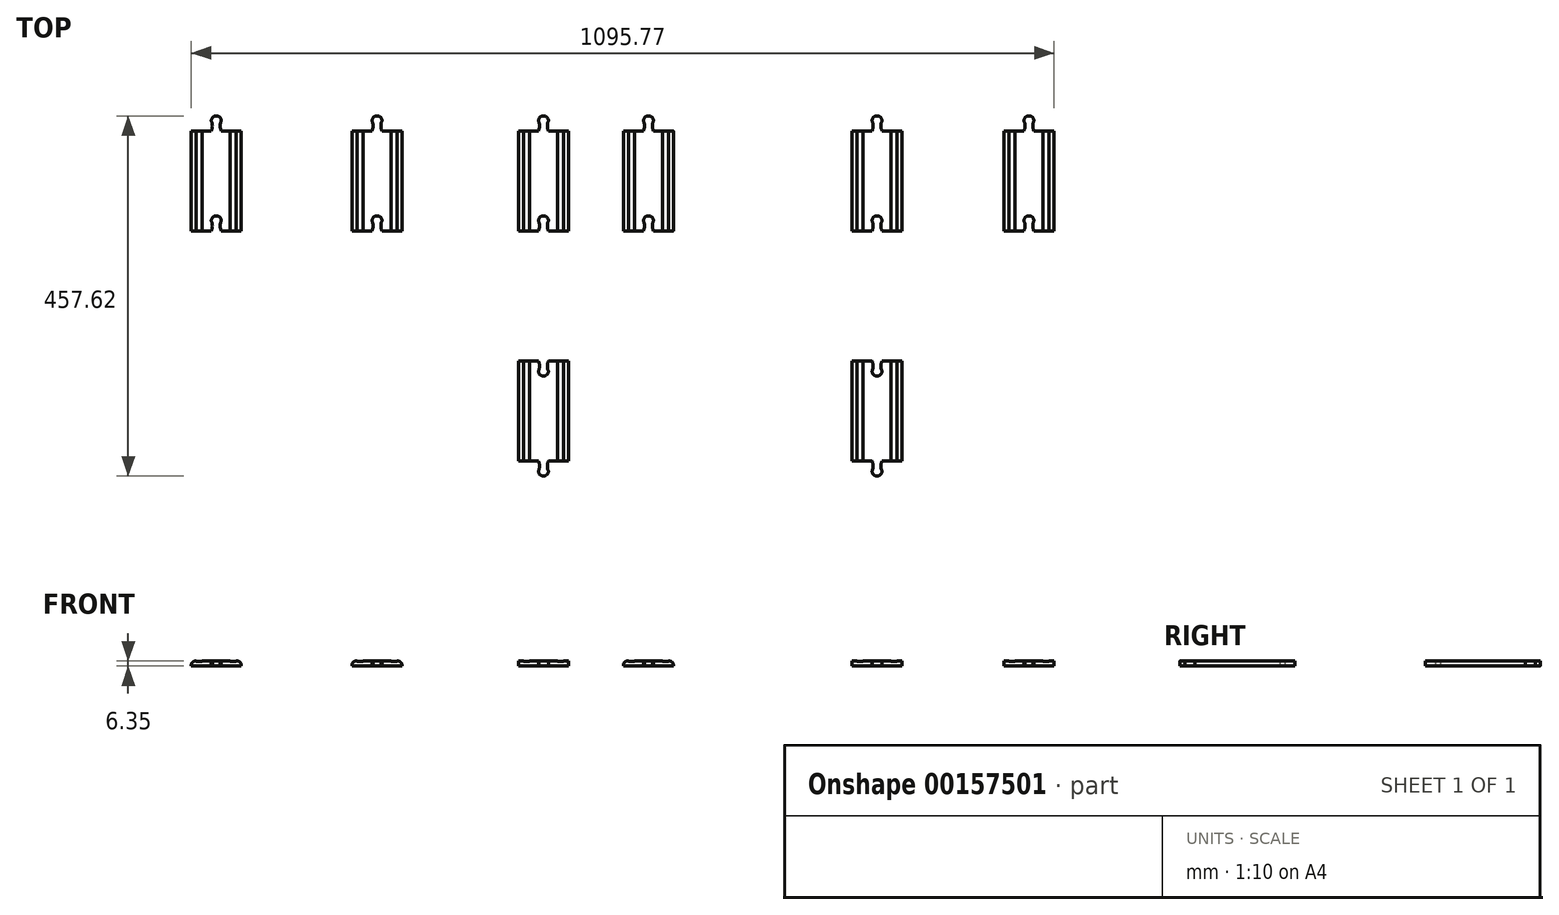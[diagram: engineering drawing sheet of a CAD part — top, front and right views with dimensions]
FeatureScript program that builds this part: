
annotation { "Feature Type Name" : "Feature", "Feature Type Description" : "" }
export const myFeature = defineFeature(function(context is Context, id is Id, definition is map)
    precondition{}
    {
        {
            var Q0;
            Q0=qCreatedBy(makeId("Top.planeOp"),FACE);
            var sketch = newSketch(context, id + "F0", { "sketchPlane" : qUnion([Q0])});
            skLineSegment(sketch, "E0", {"start": v(-44.88, 90.72) * mm, "end": v(-44.88, -36.28) * mm});
            skLineSegment(sketch, "E1", {"start": v(-44.88, -36.28) * mm, "end": v(-19.48, -36.28) * mm});
            skLineSegment(sketch, "E2", {"start": v(18.62, -36.28) * mm, "end": v(18.62, 90.72) * mm});
            skLineSegment(sketch, "E3", {"start": v(18.62, 90.72) * mm, "end": v(-6.78, 90.72) * mm});
            skArc(sketch, "E4", {"start": v(-6.78, 103.42) * mm, "mid": v(-13.13, 109.77) * mm, "end": v(-19.48, 103.42) * mm});
            skArc(sketch, "E5", {"start": v(-6.78, 103.42) * mm, "mid": v(-8.16, 97.07) * mm, "end": v(-6.78, 90.72) * mm});
            skArc(sketch, "E6.MirrorCS", {"start": v(-19.48, 103.42) * mm, "mid": v(-18.09, 97.07) * mm, "end": v(-19.48, 90.72) * mm});
            skArc(sketch, "E7", {"start": v(-6.78, -23.58) * mm, "mid": v(-13.13, -17.23) * mm, "end": v(-19.48, -23.58) * mm});
            skPoint(sketch, "E8.start.orphan", {"position": v(-13.13, -36.28) * mm});
            skArc(sketch, "E9", {"start": v(-6.78, -23.58) * mm, "mid": v(-8.16, -29.93) * mm, "end": v(-6.78, -36.28) * mm});
            skArc(sketch, "E10.MirrorCS", {"start": v(-19.48, -23.58) * mm, "mid": v(-18.09, -29.93) * mm, "end": v(-19.48, -36.28) * mm});
            skLineSegment(sketch, "E11.trimOffspring", {"start": v(-6.78, -36.28) * mm, "end": v(18.62, -36.28) * mm});
            skArc(sketch, "E12.MirrorCS", {"start": v(80.5, 103.42) * mm, "mid": v(81.9, 97.07) * mm, "end": v(80.5, 90.72) * mm});
            skLineSegment(sketch, "E13.MirrorCS", {"start": v(55.1, 90.72) * mm, "end": v(80.5, 90.72) * mm});
            skLineSegment(sketch, "E14.MirrorCS", {"start": v(118.6, 90.72) * mm, "end": v(118.6, -36.28) * mm});
            skLineSegment(sketch, "E15.MirrorCS", {"start": v(80.5, -36.28) * mm, "end": v(55.1, -36.28) * mm});
            skPoint(sketch, "E16.MirrorP", {"position": v(86.86, -36.28) * mm});
            skArc(sketch, "E17.MirrorCS", {"start": v(80.5, -23.58) * mm, "mid": v(81.9, -29.93) * mm, "end": v(80.5, -36.28) * mm});
            skArc(sketch, "E18.MirrorCS", {"start": v(80.5, 103.42) * mm, "mid": v(86.86, 109.77) * mm, "end": v(93.2, 103.42) * mm});
            skLineSegment(sketch, "E19.MirrorCS", {"start": v(55.1, -36.28) * mm, "end": v(55.1, 90.72) * mm});
            skArc(sketch, "E20.MirrorCS", {"start": v(93.2, -23.58) * mm, "mid": v(91.82, -29.93) * mm, "end": v(93.2, -36.28) * mm});
            skArc(sketch, "E21.MirrorCS", {"start": v(80.5, -23.58) * mm, "mid": v(86.86, -17.23) * mm, "end": v(93.2, -23.58) * mm});
            skLineSegment(sketch, "E22.MirrorCS", {"start": v(118.6, -36.28) * mm, "end": v(93.2, -36.28) * mm});
            skArc(sketch, "E23.MirrorCS", {"start": v(93.2, 103.42) * mm, "mid": v(91.82, 97.07) * mm, "end": v(93.2, 90.72) * mm});
            skArc(sketch, "E24.MirrorCS", {"start": v(197.37, -23.58) * mm, "mid": v(195.98, -29.93) * mm, "end": v(197.37, -36.28) * mm});
            skArc(sketch, "E25.MirrorCS", {"start": v(184.67, -23.58) * mm, "mid": v(186.06, -29.93) * mm, "end": v(184.67, -36.28) * mm});
            skArc(sketch, "E26.MirrorCS", {"start": v(184.67, 103.42) * mm, "mid": v(186.06, 97.07) * mm, "end": v(184.67, 90.72) * mm});
            skArc(sketch, "E27.MirrorCS", {"start": v(197.37, -23.58) * mm, "mid": v(191.02, -17.23) * mm, "end": v(184.67, -23.58) * mm});
            skArc(sketch, "E28.MirrorCS", {"start": v(197.37, 103.42) * mm, "mid": v(195.98, 97.07) * mm, "end": v(197.37, 90.72) * mm});
            skLineSegment(sketch, "E29.MirrorCS", {"start": v(197.37, -36.28) * mm, "end": v(222.77, -36.28) * mm});
            skArc(sketch, "E30.MirrorCS", {"start": v(197.37, 103.42) * mm, "mid": v(191.02, 109.77) * mm, "end": v(184.67, 103.42) * mm});
            skLineSegment(sketch, "E31.MirrorCS", {"start": v(159.27, -36.28) * mm, "end": v(184.67, -36.28) * mm});
            skLineSegment(sketch, "E32.MirrorCS", {"start": v(222.77, 90.72) * mm, "end": v(197.37, 90.72) * mm});
            skLineSegment(sketch, "E33.MirrorCS", {"start": v(222.77, -36.28) * mm, "end": v(222.77, 90.72) * mm});
            skPoint(sketch, "E34.MirrorP", {"position": v(191.02, -36.28) * mm});
            skLineSegment(sketch, "E35.MirrorCS", {"start": v(159.27, 90.72) * mm, "end": v(159.27, -36.28) * mm});
            skArc(sketch, "E36.MirrorCS", {"start": v(408.77, -23.58) * mm, "mid": v(407.39, -29.93) * mm, "end": v(408.77, -36.28) * mm});
            skArc(sketch, "E37.MirrorCS", {"start": v(396.07, -23.58) * mm, "mid": v(397.46, -29.93) * mm, "end": v(396.07, -36.28) * mm});
            skArc(sketch, "E38.MirrorCS", {"start": v(396.07, 103.42) * mm, "mid": v(402.42, 109.77) * mm, "end": v(408.77, 103.42) * mm});
            skLineSegment(sketch, "E39.MirrorCS", {"start": v(396.07, -36.28) * mm, "end": v(370.67, -36.28) * mm});
            skLineSegment(sketch, "E40.MirrorCS", {"start": v(434.17, -36.28) * mm, "end": v(408.77, -36.28) * mm});
            skArc(sketch, "E41.MirrorCS", {"start": v(396.07, -23.58) * mm, "mid": v(402.42, -17.23) * mm, "end": v(408.77, -23.58) * mm});
            skArc(sketch, "E42.MirrorCS", {"start": v(408.77, 103.42) * mm, "mid": v(407.39, 97.07) * mm, "end": v(408.77, 90.72) * mm});
            skArc(sketch, "E43.MirrorCS", {"start": v(396.07, 103.42) * mm, "mid": v(397.46, 97.07) * mm, "end": v(396.07, 90.72) * mm});
            skLineSegment(sketch, "E44.MirrorCS", {"start": v(370.67, 90.72) * mm, "end": v(396.07, 90.72) * mm});
            skLineSegment(sketch, "E45.MirrorCS", {"start": v(370.67, -36.28) * mm, "end": v(370.67, 90.72) * mm});
            skPoint(sketch, "E46.MirrorP", {"position": v(402.42, -36.28) * mm});
            skLineSegment(sketch, "E47.MirrorCS", {"start": v(434.17, 90.72) * mm, "end": v(434.17, -36.28) * mm});
            skArc(sketch, "E48.MirrorCS", {"start": v(542.2, 103.42) * mm, "mid": v(540.8, 97.07) * mm, "end": v(542.2, 90.72) * mm});
            skArc(sketch, "E49.MirrorCS", {"start": v(542.2, -23.58) * mm, "mid": v(540.8, -29.93) * mm, "end": v(542.2, -36.28) * mm});
            skArc(sketch, "E50.MirrorCS", {"start": v(542.2, 103.42) * mm, "mid": v(535.84, 109.77) * mm, "end": v(529.5, 103.42) * mm});
            skArc(sketch, "E51.MirrorCS", {"start": v(529.5, 103.42) * mm, "mid": v(530.88, 97.07) * mm, "end": v(529.5, 90.72) * mm});
            skArc(sketch, "E52.MirrorCS", {"start": v(529.5, -23.58) * mm, "mid": v(530.88, -29.93) * mm, "end": v(529.5, -36.28) * mm});
            skLineSegment(sketch, "E53.MirrorCS", {"start": v(567.6, 90.72) * mm, "end": v(542.2, 90.72) * mm});
            skArc(sketch, "E54.MirrorCS", {"start": v(542.2, -23.58) * mm, "mid": v(535.84, -17.23) * mm, "end": v(529.5, -23.58) * mm});
            skLineSegment(sketch, "E55.MirrorCS", {"start": v(504.1, -36.28) * mm, "end": v(529.5, -36.28) * mm});
            skLineSegment(sketch, "E56.MirrorCS", {"start": v(542.2, -36.28) * mm, "end": v(567.6, -36.28) * mm});
            skLineSegment(sketch, "E57.MirrorCS", {"start": v(504.1, 90.72) * mm, "end": v(504.1, -36.28) * mm});
            skLineSegment(sketch, "E58.MirrorCS", {"start": v(567.6, -36.28) * mm, "end": v(567.6, 90.72) * mm});
            skPoint(sketch, "E59.MirrorP", {"position": v(535.84, -36.28) * mm});
            skArc(sketch, "E60.MirrorCS", {"start": v(832.53, -23.58) * mm, "mid": v(831.14, -29.93) * mm, "end": v(832.53, -36.28) * mm});
            skArc(sketch, "E61.MirrorCS", {"start": v(819.83, -23.58) * mm, "mid": v(821.22, -29.93) * mm, "end": v(819.83, -36.28) * mm});
            skArc(sketch, "E62.MirrorCS", {"start": v(819.83, -23.58) * mm, "mid": v(826.18, -17.23) * mm, "end": v(832.53, -23.58) * mm});
            skLineSegment(sketch, "E63.MirrorCS", {"start": v(857.93, -36.28) * mm, "end": v(832.53, -36.28) * mm});
            skArc(sketch, "E64.MirrorCS", {"start": v(819.83, 103.42) * mm, "mid": v(821.22, 97.07) * mm, "end": v(819.83, 90.72) * mm});
            skArc(sketch, "E65.MirrorCS", {"start": v(832.53, 103.42) * mm, "mid": v(831.14, 97.07) * mm, "end": v(832.53, 90.72) * mm});
            skArc(sketch, "E66.MirrorCS", {"start": v(819.83, 103.42) * mm, "mid": v(826.18, 109.77) * mm, "end": v(832.53, 103.42) * mm});
            skLineSegment(sketch, "E67.MirrorCS", {"start": v(819.83, -36.28) * mm, "end": v(794.43, -36.28) * mm});
            skLineSegment(sketch, "E68.MirrorCS", {"start": v(794.43, 90.72) * mm, "end": v(819.83, 90.72) * mm});
            skPoint(sketch, "E69.MirrorP", {"position": v(826.18, -36.28) * mm});
            skLineSegment(sketch, "E70.MirrorCS", {"start": v(857.93, 90.72) * mm, "end": v(857.93, -36.28) * mm});
            skLineSegment(sketch, "E71.MirrorCS", {"start": v(794.43, -36.28) * mm, "end": v(794.43, 90.72) * mm});
            skArc(sketch, "E72.MirrorCS", {"start": v(819.83, -341.5) * mm, "mid": v(821.22, -335.15) * mm, "end": v(819.83, -328.8) * mm});
            skArc(sketch, "E73.MirrorCS", {"start": v(396.07, -214.5) * mm, "mid": v(397.46, -208.15) * mm, "end": v(396.07, -201.8) * mm});
            skArc(sketch, "E74.MirrorCS", {"start": v(93.2, -214.5) * mm, "mid": v(91.82, -208.15) * mm, "end": v(93.2, -201.8) * mm});
            skArc(sketch, "E75.MirrorCS", {"start": v(832.53, -341.5) * mm, "mid": v(831.14, -335.15) * mm, "end": v(832.53, -328.8) * mm});
            skArc(sketch, "E76.MirrorCS", {"start": v(408.77, -214.5) * mm, "mid": v(407.39, -208.15) * mm, "end": v(408.77, -201.8) * mm});
            skArc(sketch, "E77.MirrorCS", {"start": v(197.37, -214.5) * mm, "mid": v(191.02, -220.85) * mm, "end": v(184.67, -214.5) * mm});
            skArc(sketch, "E78.MirrorCS", {"start": v(80.5, -214.5) * mm, "mid": v(86.86, -220.85) * mm, "end": v(93.2, -214.5) * mm});
            skArc(sketch, "E79.MirrorCS", {"start": v(819.83, -341.5) * mm, "mid": v(826.18, -347.85) * mm, "end": v(832.53, -341.5) * mm});
            skArc(sketch, "E80.MirrorCS", {"start": v(819.83, -214.5) * mm, "mid": v(821.22, -208.15) * mm, "end": v(819.83, -201.8) * mm});
            skArc(sketch, "E81.MirrorCS", {"start": v(542.2, -214.5) * mm, "mid": v(540.8, -208.15) * mm, "end": v(542.2, -201.8) * mm});
            skArc(sketch, "E82.MirrorCS", {"start": v(197.37, -214.5) * mm, "mid": v(195.98, -208.15) * mm, "end": v(197.37, -201.8) * mm});
            skArc(sketch, "E83.MirrorCS", {"start": v(80.5, -214.5) * mm, "mid": v(81.9, -208.15) * mm, "end": v(80.5, -201.8) * mm});
            skArc(sketch, "E84.MirrorCS", {"start": v(832.53, -214.5) * mm, "mid": v(831.14, -208.15) * mm, "end": v(832.53, -201.8) * mm});
            skArc(sketch, "E85.MirrorCS", {"start": v(184.67, -214.5) * mm, "mid": v(186.06, -208.15) * mm, "end": v(184.67, -201.8) * mm});
            skArc(sketch, "E86.MirrorCS", {"start": v(529.5, -214.5) * mm, "mid": v(530.88, -208.15) * mm, "end": v(529.5, -201.8) * mm});
            skLineSegment(sketch, "E87.MirrorCS", {"start": v(197.37, -201.8) * mm, "end": v(222.77, -201.8) * mm});
            skArc(sketch, "E88.MirrorCS", {"start": v(542.2, -214.5) * mm, "mid": v(535.84, -220.85) * mm, "end": v(529.5, -214.5) * mm});
            skArc(sketch, "E89.MirrorCS", {"start": v(197.37, -341.5) * mm, "mid": v(195.98, -335.15) * mm, "end": v(197.37, -328.8) * mm});
            skLineSegment(sketch, "E90.MirrorCS", {"start": v(857.93, -201.8) * mm, "end": v(832.53, -201.8) * mm});
            skArc(sketch, "E91.MirrorCS", {"start": v(80.5, -341.5) * mm, "mid": v(86.86, -347.85) * mm, "end": v(93.2, -341.5) * mm});
            skLineSegment(sketch, "E92.MirrorCS", {"start": v(504.1, -201.8) * mm, "end": v(529.5, -201.8) * mm});
            skArc(sketch, "E93.MirrorCS", {"start": v(396.07, -341.5) * mm, "mid": v(402.42, -347.85) * mm, "end": v(408.77, -341.5) * mm});
            skArc(sketch, "E94.MirrorCS", {"start": v(542.2, -341.5) * mm, "mid": v(540.8, -335.15) * mm, "end": v(542.2, -328.8) * mm});
            skArc(sketch, "E95.MirrorCS", {"start": v(197.37, -341.5) * mm, "mid": v(191.02, -347.85) * mm, "end": v(184.67, -341.5) * mm});
            skLineSegment(sketch, "E96.MirrorCS", {"start": v(567.6, -328.8) * mm, "end": v(542.2, -328.8) * mm});
            skLineSegment(sketch, "E97.MirrorCS", {"start": v(370.67, -328.8) * mm, "end": v(396.07, -328.8) * mm});
            skArc(sketch, "E98.MirrorCS", {"start": v(819.83, -214.5) * mm, "mid": v(826.18, -220.85) * mm, "end": v(832.53, -214.5) * mm});
            skLineSegment(sketch, "E99.MirrorCS", {"start": v(396.07, -201.8) * mm, "end": v(370.67, -201.8) * mm});
            skLineSegment(sketch, "E100.MirrorCS", {"start": v(542.2, -201.8) * mm, "end": v(567.6, -201.8) * mm});
            skArc(sketch, "E101.MirrorCS", {"start": v(93.2, -341.5) * mm, "mid": v(91.82, -335.15) * mm, "end": v(93.2, -328.8) * mm});
            skArc(sketch, "E102.MirrorCS", {"start": v(396.07, -341.5) * mm, "mid": v(397.46, -335.15) * mm, "end": v(396.07, -328.8) * mm});
            skLineSegment(sketch, "E103.MirrorCS", {"start": v(794.43, -328.8) * mm, "end": v(819.83, -328.8) * mm});
            skArc(sketch, "E104.MirrorCS", {"start": v(529.5, -341.5) * mm, "mid": v(530.88, -335.15) * mm, "end": v(529.5, -328.8) * mm});
            skArc(sketch, "E105.MirrorCS", {"start": v(184.67, -341.5) * mm, "mid": v(186.06, -335.15) * mm, "end": v(184.67, -328.8) * mm});
            skArc(sketch, "E106.MirrorCS", {"start": v(396.07, -214.5) * mm, "mid": v(402.42, -220.85) * mm, "end": v(408.77, -214.5) * mm});
            skLineSegment(sketch, "E107.MirrorCS", {"start": v(55.1, -328.8) * mm, "end": v(80.5, -328.8) * mm});
            skLineSegment(sketch, "E108.MirrorCS", {"start": v(159.27, -201.8) * mm, "end": v(184.67, -201.8) * mm});
            skLineSegment(sketch, "E109.MirrorCS", {"start": v(80.5, -201.8) * mm, "end": v(55.1, -201.8) * mm});
            skLineSegment(sketch, "E110.MirrorCS", {"start": v(434.17, -201.8) * mm, "end": v(408.77, -201.8) * mm});
            skLineSegment(sketch, "E111.MirrorCS", {"start": v(819.83, -201.8) * mm, "end": v(794.43, -201.8) * mm});
            skArc(sketch, "E112.MirrorCS", {"start": v(408.77, -341.5) * mm, "mid": v(407.39, -335.15) * mm, "end": v(408.77, -328.8) * mm});
            skLineSegment(sketch, "E113.MirrorCS", {"start": v(222.77, -328.8) * mm, "end": v(197.37, -328.8) * mm});
            skArc(sketch, "E114.MirrorCS", {"start": v(80.5, -341.5) * mm, "mid": v(81.9, -335.15) * mm, "end": v(80.5, -328.8) * mm});
            skLineSegment(sketch, "E115.MirrorCS", {"start": v(118.6, -201.8) * mm, "end": v(93.2, -201.8) * mm});
            skArc(sketch, "E116.MirrorCS", {"start": v(542.2, -341.5) * mm, "mid": v(535.84, -347.85) * mm, "end": v(529.5, -341.5) * mm});
            skLineSegment(sketch, "E117.MirrorCS", {"start": v(434.17, -328.8) * mm, "end": v(434.17, -201.8) * mm});
            skLineSegment(sketch, "E118.MirrorCS", {"start": v(55.1, -201.8) * mm, "end": v(55.1, -328.8) * mm});
            skLineSegment(sketch, "E119.MirrorCS", {"start": v(370.67, -201.8) * mm, "end": v(370.67, -328.8) * mm});
            skPoint(sketch, "E120.MirrorP", {"position": v(86.86, -201.8) * mm});
            skLineSegment(sketch, "E121.MirrorCS", {"start": v(794.43, -201.8) * mm, "end": v(794.43, -328.8) * mm});
            skPoint(sketch, "E122.MirrorP", {"position": v(191.02, -201.8) * mm});
            skPoint(sketch, "E123.MirrorP", {"position": v(535.84, -201.8) * mm});
            skPoint(sketch, "E124.MirrorP", {"position": v(402.42, -201.8) * mm});
            skLineSegment(sketch, "E125.MirrorCS", {"start": v(567.6, -201.8) * mm, "end": v(567.6, -328.8) * mm});
            skLineSegment(sketch, "E126.MirrorCS", {"start": v(222.77, -201.8) * mm, "end": v(222.77, -328.8) * mm});
            skLineSegment(sketch, "E127.MirrorCS", {"start": v(118.6, -328.8) * mm, "end": v(118.6, -201.8) * mm});
            skPoint(sketch, "E128.MirrorP", {"position": v(826.18, -201.8) * mm});
            skLineSegment(sketch, "E129.MirrorCS", {"start": v(504.1, -328.8) * mm, "end": v(504.1, -201.8) * mm});
            skLineSegment(sketch, "E130.MirrorCS", {"start": v(159.27, -328.8) * mm, "end": v(159.27, -201.8) * mm});
            skLineSegment(sketch, "E131.MirrorCS", {"start": v(857.93, -328.8) * mm, "end": v(857.93, -201.8) * mm});
            skArc(sketch, "E132.MirrorCS", {"start": v(-6.78, -341.5) * mm, "mid": v(-13.13, -347.85) * mm, "end": v(-19.48, -341.5) * mm});
            skArc(sketch, "E133.MirrorCS", {"start": v(-19.48, -214.5) * mm, "mid": v(-18.09, -208.15) * mm, "end": v(-19.48, -201.8) * mm});
            skArc(sketch, "E134.MirrorCS", {"start": v(-6.78, -214.5) * mm, "mid": v(-13.13, -220.85) * mm, "end": v(-19.48, -214.5) * mm});
            skLineSegment(sketch, "E135.MirrorCS", {"start": v(-6.78, -201.8) * mm, "end": v(18.62, -201.8) * mm});
            skArc(sketch, "E136.MirrorCS", {"start": v(-6.78, -214.5) * mm, "mid": v(-8.16, -208.15) * mm, "end": v(-6.78, -201.8) * mm});
            skArc(sketch, "E137.MirrorCS", {"start": v(-19.48, -341.5) * mm, "mid": v(-18.09, -335.15) * mm, "end": v(-19.48, -328.8) * mm});
            skArc(sketch, "E138.MirrorCS", {"start": v(-6.78, -341.5) * mm, "mid": v(-8.16, -335.15) * mm, "end": v(-6.78, -328.8) * mm});
            skLineSegment(sketch, "E139.MirrorCS", {"start": v(18.62, -328.8) * mm, "end": v(-6.78, -328.8) * mm});
            skLineSegment(sketch, "E140.MirrorCS", {"start": v(-44.88, -201.8) * mm, "end": v(-19.48, -201.8) * mm});
            skLineSegment(sketch, "E141.MirrorCS", {"start": v(18.62, -201.8) * mm, "end": v(18.62, -328.8) * mm});
            skLineSegment(sketch, "E142.MirrorCS", {"start": v(-44.88, -328.8) * mm, "end": v(-44.88, -201.8) * mm});
            skPoint(sketch, "E143.MirrorP", {"position": v(-13.13, -201.8) * mm});
            skLineSegment(sketch, "E144.trimOffspring", {"start": v(-19.48, 90.72) * mm, "end": v(-44.88, 90.72) * mm});
            skLineSegment(sketch, "E145.trimOffspring", {"start": v(93.2, 90.72) * mm, "end": v(118.6, 90.72) * mm});
            skLineSegment(sketch, "E146.trimOffspring", {"start": v(184.67, 90.72) * mm, "end": v(159.27, 90.72) * mm});
            skLineSegment(sketch, "E147.trimOffspring", {"start": v(408.77, 90.72) * mm, "end": v(434.17, 90.72) * mm});
            skLineSegment(sketch, "E148.trimOffspring", {"start": v(529.5, 90.72) * mm, "end": v(504.1, 90.72) * mm});
            skLineSegment(sketch, "E149.trimOffspring", {"start": v(832.53, 90.72) * mm, "end": v(857.93, 90.72) * mm});
            skLineSegment(sketch, "E150.trimOffspring", {"start": v(832.53, -328.8) * mm, "end": v(857.93, -328.8) * mm});
            skLineSegment(sketch, "E151.trimOffspring", {"start": v(529.5, -328.8) * mm, "end": v(504.1, -328.8) * mm});
            skLineSegment(sketch, "E152.trimOffspring", {"start": v(408.77, -328.8) * mm, "end": v(434.17, -328.8) * mm});
            skLineSegment(sketch, "E153.trimOffspring", {"start": v(184.67, -328.8) * mm, "end": v(159.27, -328.8) * mm});
            skLineSegment(sketch, "E154.trimOffspring", {"start": v(93.2, -328.8) * mm, "end": v(118.6, -328.8) * mm});
            skLineSegment(sketch, "E155.trimOffspring", {"start": v(-19.48, -328.8) * mm, "end": v(-44.88, -328.8) * mm});
            skLineSegment(sketch, "E156", {"start": v(922.66, 120.17) * mm, "end": v(922.66, -61.86) * mm});
            skArc(sketch, "E157.MirrorCS", {"start": v(1025.49, -23.58) * mm, "mid": v(1024.1, -29.93) * mm, "end": v(1025.49, -36.28) * mm});
            skArc(sketch, "E158.MirrorCS", {"start": v(1012.79, -23.58) * mm, "mid": v(1014.17, -29.93) * mm, "end": v(1012.79, -36.28) * mm});
            skArc(sketch, "E159.MirrorCS", {"start": v(1025.49, 103.42) * mm, "mid": v(1024.1, 97.07) * mm, "end": v(1025.49, 90.72) * mm});
            skArc(sketch, "E160.MirrorCS", {"start": v(1012.79, 103.42) * mm, "mid": v(1014.17, 97.07) * mm, "end": v(1012.79, 90.72) * mm});
            skLineSegment(sketch, "E161.MirrorCS", {"start": v(1025.49, -36.28) * mm, "end": v(1050.89, -36.28) * mm});
            skLineSegment(sketch, "E162.MirrorCS", {"start": v(1050.89, 90.72) * mm, "end": v(1025.49, 90.72) * mm});
            skArc(sketch, "E163.MirrorCS", {"start": v(1025.49, -23.58) * mm, "mid": v(1019.14, -17.23) * mm, "end": v(1012.79, -23.58) * mm});
            skArc(sketch, "E164.MirrorCS", {"start": v(1025.49, 103.42) * mm, "mid": v(1019.14, 109.77) * mm, "end": v(1012.79, 103.42) * mm});
            skLineSegment(sketch, "E165.MirrorCS", {"start": v(1012.79, 90.72) * mm, "end": v(987.39, 90.72) * mm});
            skLineSegment(sketch, "E166.MirrorCS", {"start": v(987.39, -36.28) * mm, "end": v(1012.79, -36.28) * mm});
            skPoint(sketch, "E167.MirrorP", {"position": v(1019.14, -36.28) * mm});
            skLineSegment(sketch, "E168.MirrorCS", {"start": v(987.39, 90.72) * mm, "end": v(987.39, -36.28) * mm});
            skLineSegment(sketch, "E169.MirrorCS", {"start": v(1050.89, -36.28) * mm, "end": v(1050.89, 90.72) * mm});
            skSolve(sketch);
        }
        {
            var Q0;
            Q0=makeQuery(id+"F0.imprint","IMPRINT",FACE,{"disambiguationData":[TD([[makeQuery(id+"F0.imprint","IMPRINT",EDGE,{"derivedFrom":sQuery(id+"F0.wireOp",EDGE,"E0")}),1.0]])]});
            var Q1;
            Q1=makeQuery(id+"F0.imprint","IMPRINT",FACE,{"disambiguationData":[TD([[makeQuery(id+"F0.imprint","IMPRINT",EDGE,{"derivedFrom":sQuery(id+"F0.wireOp",EDGE,"E12.MirrorCS")}),1.0]])]});
            var Q2;
            Q2=makeQuery(id+"F0.imprint","IMPRINT",FACE,{"disambiguationData":[TD([[makeQuery(id+"F0.imprint","IMPRINT",EDGE,{"derivedFrom":sQuery(id+"F0.wireOp",EDGE,"E24.MirrorCS")}),1.0]])]});
            var Q3;
            Q3=makeQuery(id+"F0.imprint","IMPRINT",FACE,{"disambiguationData":[TD([[makeQuery(id+"F0.imprint","IMPRINT",EDGE,{"derivedFrom":sQuery(id+"F0.wireOp",EDGE,"E36.MirrorCS")}),1.0]])]});
            var Q4;
            Q4=makeQuery(id+"F0.imprint","IMPRINT",FACE,{"disambiguationData":[TD([[makeQuery(id+"F0.imprint","IMPRINT",EDGE,{"derivedFrom":sQuery(id+"F0.wireOp",EDGE,"E48.MirrorCS")}),-1.0]])]});
            var Q5;
            Q5=makeQuery(id+"F0.imprint","IMPRINT",FACE,{"disambiguationData":[TD([[makeQuery(id+"F0.imprint","IMPRINT",EDGE,{"derivedFrom":sQuery(id+"F0.wireOp",EDGE,"E132.MirrorCS")}),-1.0]])]});
            var Q6;
            Q6=makeQuery(id+"F0.imprint","IMPRINT",FACE,{"disambiguationData":[TD([[makeQuery(id+"F0.imprint","IMPRINT",EDGE,{"derivedFrom":sQuery(id+"F0.wireOp",EDGE,"E74.MirrorCS")}),-1.0]])]});
            var Q7;
            Q7=makeQuery(id+"F0.imprint","IMPRINT",FACE,{"disambiguationData":[TD([[makeQuery(id+"F0.imprint","IMPRINT",EDGE,{"derivedFrom":sQuery(id+"F0.wireOp",EDGE,"E77.MirrorCS")}),1.0]])]});
            var Q8;
            Q8=makeQuery(id+"F0.imprint","IMPRINT",FACE,{"disambiguationData":[TD([[makeQuery(id+"F0.imprint","IMPRINT",EDGE,{"derivedFrom":sQuery(id+"F0.wireOp",EDGE,"E73.MirrorCS")}),1.0]])]});
            var Q9;
            Q9=makeQuery(id+"F0.imprint","IMPRINT",FACE,{"disambiguationData":[TD([[makeQuery(id+"F0.imprint","IMPRINT",EDGE,{"derivedFrom":sQuery(id+"F0.wireOp",EDGE,"E81.MirrorCS")}),-1.0]])]});
            var Q10;
            Q10=makeQuery(id+"F0.imprint","IMPRINT",FACE,{"disambiguationData":[TD([[makeQuery(id+"F0.imprint","IMPRINT",EDGE,{"derivedFrom":sQuery(id+"F0.wireOp",EDGE,"E60.MirrorCS")}),1.0]])]});
            var Q11;
            Q11=makeQuery(id+"F0.imprint","IMPRINT",FACE,{"disambiguationData":[TD([[makeQuery(id+"F0.imprint","IMPRINT",EDGE,{"derivedFrom":sQuery(id+"F0.wireOp",EDGE,"E72.MirrorCS")}),-1.0]])]});
            var Q12;
            Q12=makeQuery(id+"F0.imprint","IMPRINT",FACE,{"disambiguationData":[TD([[makeQuery(id+"F0.imprint","IMPRINT",EDGE,{"derivedFrom":sQuery(id+"F0.wireOp",EDGE,"E157.MirrorCS")}),1.0]])]});
            extrude(context, id + "F1", {"entities" : qUnion([Q0, Q1, Q2, Q3, Q4, Q5, Q6, Q7, Q8, Q9, Q10, Q11, Q12]), "depth" : 6.35 * mm});
        }
        {
            var Q0;
            Q0=makeQuery(id+"F1.opExtrude","CAP_FACE",FACE,{"disambiguationData":[OSD([sQuery(id+"F0.wireOp",EDGE,"E0"),sQuery(id+"F0.wireOp",EDGE,"E1"),sQuery(id+"F0.wireOp",EDGE,"E2"),sQuery(id+"F0.wireOp",EDGE,"E3"),sQuery(id+"F0.wireOp",EDGE,"E4"),sQuery(id+"F0.wireOp",EDGE,"E5"),sQuery(id+"F0.wireOp",EDGE,"E6.MirrorCS"),sQuery(id+"F0.wireOp",EDGE,"E7"),sQuery(id+"F0.wireOp",EDGE,"E9"),sQuery(id+"F0.wireOp",EDGE,"E10.MirrorCS"),sQuery(id+"F0.wireOp",EDGE,"E11.trimOffspring"),sQuery(id+"F0.wireOp",EDGE,"E144.trimOffspring")])],"isStart":false});
            var sketch = newSketch(context, id + "F2", { "sketchPlane" : qUnion([Q0])});
            skLineSegment(sketch, "E170.12", {"start": v(857.93, -328.8) * mm, "end": v(857.93, -201.8) * mm});
            skLineSegment(sketch, "E170.13", {"start": v(794.43, -201.8) * mm, "end": v(794.43, -328.8) * mm});
            skLineSegment(sketch, "E171.0", {"start": v(-38.53, 90.72) * mm, "end": v(-38.53, -36.28) * mm});
            skLineSegment(sketch, "E172.0", {"start": v(-30.9, 90.72) * mm, "end": v(-30.9, -36.28) * mm});
            skLineSegment(sketch, "E173", {"start": v(4.65, 90.72) * mm, "end": v(4.65, -36.28) * mm});
            skLineSegment(sketch, "E174", {"start": v(12.27, 90.72) * mm, "end": v(12.27, -36.28) * mm});
            skLineSegment(sketch, "E175", {"start": v(-38.53, -36.28) * mm, "end": v(-30.9, -36.28) * mm});
            skLineSegment(sketch, "E176", {"start": v(-30.9, 90.72) * mm, "end": v(-38.53, 90.72) * mm});
            skLineSegment(sketch, "E177", {"start": v(4.65, 90.72) * mm, "end": v(12.27, 90.72) * mm});
            skLineSegment(sketch, "E178", {"start": v(12.27, -36.28) * mm, "end": v(4.65, -36.28) * mm});
            skLineSegment(sketch, "E179.MirrorCS", {"start": v(61.46, 90.72) * mm, "end": v(61.46, -36.28) * mm});
            skLineSegment(sketch, "E180.MirrorCS", {"start": v(69.08, 90.72) * mm, "end": v(69.08, -36.28) * mm});
            skLineSegment(sketch, "E181.MirrorCS", {"start": v(61.46, -36.28) * mm, "end": v(69.08, -36.28) * mm});
            skLineSegment(sketch, "E182.MirrorCS", {"start": v(69.08, 90.72) * mm, "end": v(61.46, 90.72) * mm});
            skLineSegment(sketch, "E183.MirrorCS", {"start": v(112.26, -36.28) * mm, "end": v(104.64, -36.28) * mm});
            skLineSegment(sketch, "E184.MirrorCS", {"start": v(104.64, 90.72) * mm, "end": v(104.64, -36.28) * mm});
            skLineSegment(sketch, "E185.MirrorCS", {"start": v(112.26, 90.72) * mm, "end": v(112.26, -36.28) * mm});
            skLineSegment(sketch, "E186.MirrorCS", {"start": v(104.64, 90.72) * mm, "end": v(112.26, 90.72) * mm});
            skLineSegment(sketch, "E187.MirrorCS", {"start": v(165.62, 90.72) * mm, "end": v(165.62, -36.28) * mm});
            skLineSegment(sketch, "E188.MirrorCS", {"start": v(173.24, 90.72) * mm, "end": v(173.24, -36.28) * mm});
            skLineSegment(sketch, "E189.MirrorCS", {"start": v(208.8, 90.72) * mm, "end": v(208.8, -36.28) * mm});
            skLineSegment(sketch, "E190.MirrorCS", {"start": v(216.42, 90.72) * mm, "end": v(216.42, -36.28) * mm});
            skLineSegment(sketch, "E191.MirrorCS", {"start": v(173.24, 90.72) * mm, "end": v(165.62, 90.72) * mm});
            skLineSegment(sketch, "E192.MirrorCS", {"start": v(165.62, -36.28) * mm, "end": v(173.24, -36.28) * mm});
            skLineSegment(sketch, "E193.MirrorCS", {"start": v(216.42, -36.28) * mm, "end": v(208.8, -36.28) * mm});
            skLineSegment(sketch, "E194.MirrorCS", {"start": v(208.8, 90.72) * mm, "end": v(216.42, 90.72) * mm});
            skLineSegment(sketch, "E195.MirrorCS", {"start": v(377.02, 90.72) * mm, "end": v(377.02, -36.28) * mm});
            skLineSegment(sketch, "E196.MirrorCS", {"start": v(384.64, 90.72) * mm, "end": v(384.64, -36.28) * mm});
            skLineSegment(sketch, "E197.MirrorCS", {"start": v(420.2, 90.72) * mm, "end": v(420.2, -36.28) * mm});
            skLineSegment(sketch, "E198.MirrorCS", {"start": v(427.82, 90.72) * mm, "end": v(427.82, -36.28) * mm});
            skLineSegment(sketch, "E199.MirrorCS", {"start": v(420.2, 90.72) * mm, "end": v(427.82, 90.72) * mm});
            skLineSegment(sketch, "E200.MirrorCS", {"start": v(384.64, 90.72) * mm, "end": v(377.02, 90.72) * mm});
            skLineSegment(sketch, "E201.MirrorCS", {"start": v(377.02, -36.28) * mm, "end": v(384.64, -36.28) * mm});
            skLineSegment(sketch, "E202.MirrorCS", {"start": v(427.82, -36.28) * mm, "end": v(420.2, -36.28) * mm});
            skLineSegment(sketch, "E203.MirrorCS", {"start": v(510.44, 90.72) * mm, "end": v(510.44, -36.28) * mm});
            skLineSegment(sketch, "E204.MirrorCS", {"start": v(518.06, 90.72) * mm, "end": v(518.06, -36.28) * mm});
            skLineSegment(sketch, "E205.MirrorCS", {"start": v(518.06, 90.72) * mm, "end": v(510.44, 90.72) * mm});
            skLineSegment(sketch, "E206.MirrorCS", {"start": v(553.62, 90.72) * mm, "end": v(553.62, -36.28) * mm});
            skLineSegment(sketch, "E207.MirrorCS", {"start": v(561.24, 90.72) * mm, "end": v(561.24, -36.28) * mm});
            skLineSegment(sketch, "E208.MirrorCS", {"start": v(553.62, 90.72) * mm, "end": v(561.24, 90.72) * mm});
            skLineSegment(sketch, "E209.MirrorCS", {"start": v(800.78, 90.72) * mm, "end": v(800.78, -36.28) * mm});
            skLineSegment(sketch, "E210.MirrorCS", {"start": v(808.4, 90.72) * mm, "end": v(808.4, -36.28) * mm});
            skLineSegment(sketch, "E211.MirrorCS", {"start": v(808.4, 90.72) * mm, "end": v(800.78, 90.72) * mm});
            skLineSegment(sketch, "E212.MirrorCS", {"start": v(843.96, 90.72) * mm, "end": v(851.58, 90.72) * mm});
            skLineSegment(sketch, "E213.MirrorCS", {"start": v(843.96, 90.72) * mm, "end": v(843.96, -36.28) * mm});
            skLineSegment(sketch, "E214.MirrorCS", {"start": v(851.58, 90.72) * mm, "end": v(851.58, -36.28) * mm});
            skLineSegment(sketch, "E215", {"start": v(808.4, -36.28) * mm, "end": v(800.78, -36.28) * mm});
            skLineSegment(sketch, "E216", {"start": v(851.58, -36.28) * mm, "end": v(843.96, -36.28) * mm});
            skLineSegment(sketch, "E217", {"start": v(561.24, -36.28) * mm, "end": v(553.62, -36.28) * mm});
            skLineSegment(sketch, "E218", {"start": v(518.06, -36.28) * mm, "end": v(510.44, -36.28) * mm});
            skLineSegment(sketch, "E219.MirrorCS", {"start": v(427.82, -201.8) * mm, "end": v(420.2, -201.8) * mm});
            skLineSegment(sketch, "E220.MirrorCS", {"start": v(61.46, -201.8) * mm, "end": v(69.08, -201.8) * mm});
            skLineSegment(sketch, "E221.MirrorCS", {"start": v(-38.53, -201.8) * mm, "end": v(-30.9, -201.8) * mm});
            skLineSegment(sketch, "E222.MirrorCS", {"start": v(-30.9, -328.8) * mm, "end": v(-38.53, -328.8) * mm});
            skLineSegment(sketch, "E223.MirrorCS", {"start": v(165.62, -201.8) * mm, "end": v(173.24, -201.8) * mm});
            skLineSegment(sketch, "E224.MirrorCS", {"start": v(518.06, -201.8) * mm, "end": v(510.44, -201.8) * mm});
            skLineSegment(sketch, "E225.MirrorCS", {"start": v(518.06, -328.8) * mm, "end": v(510.44, -328.8) * mm});
            skLineSegment(sketch, "E226.MirrorCS", {"start": v(173.24, -328.8) * mm, "end": v(165.62, -328.8) * mm});
            skLineSegment(sketch, "E227.MirrorCS", {"start": v(851.58, -201.8) * mm, "end": v(843.96, -201.8) * mm});
            skLineSegment(sketch, "E228.MirrorCS", {"start": v(384.64, -328.8) * mm, "end": v(377.02, -328.8) * mm});
            skLineSegment(sketch, "E229.MirrorCS", {"start": v(420.2, -328.8) * mm, "end": v(427.82, -328.8) * mm});
            skLineSegment(sketch, "E230.MirrorCS", {"start": v(377.02, -201.8) * mm, "end": v(384.64, -201.8) * mm});
            skLineSegment(sketch, "E231.MirrorCS", {"start": v(208.8, -328.8) * mm, "end": v(216.42, -328.8) * mm});
            skLineSegment(sketch, "E232.MirrorCS", {"start": v(69.08, -328.8) * mm, "end": v(61.46, -328.8) * mm});
            skLineSegment(sketch, "E233.MirrorCS", {"start": v(808.4, -328.8) * mm, "end": v(800.78, -328.8) * mm});
            skLineSegment(sketch, "E234.MirrorCS", {"start": v(4.65, -328.8) * mm, "end": v(12.27, -328.8) * mm});
            skLineSegment(sketch, "E235.MirrorCS", {"start": v(112.26, -201.8) * mm, "end": v(104.64, -201.8) * mm});
            skLineSegment(sketch, "E236.MirrorCS", {"start": v(553.62, -328.8) * mm, "end": v(561.24, -328.8) * mm});
            skLineSegment(sketch, "E237.MirrorCS", {"start": v(104.64, -328.8) * mm, "end": v(112.26, -328.8) * mm});
            skLineSegment(sketch, "E238.MirrorCS", {"start": v(843.96, -328.8) * mm, "end": v(851.58, -328.8) * mm});
            skLineSegment(sketch, "E239.MirrorCS", {"start": v(216.42, -201.8) * mm, "end": v(208.8, -201.8) * mm});
            skLineSegment(sketch, "E240.MirrorCS", {"start": v(808.4, -201.8) * mm, "end": v(800.78, -201.8) * mm});
            skLineSegment(sketch, "E241.MirrorCS", {"start": v(561.24, -201.8) * mm, "end": v(553.62, -201.8) * mm});
            skLineSegment(sketch, "E242.MirrorCS", {"start": v(12.27, -201.8) * mm, "end": v(4.65, -201.8) * mm});
            skLineSegment(sketch, "E243.MirrorCS", {"start": v(12.27, -328.8) * mm, "end": v(12.27, -201.8) * mm});
            skLineSegment(sketch, "E244.MirrorCS", {"start": v(-38.53, -328.8) * mm, "end": v(-38.53, -201.8) * mm});
            skLineSegment(sketch, "E245.MirrorCS", {"start": v(377.02, -328.8) * mm, "end": v(377.02, -201.8) * mm});
            skLineSegment(sketch, "E246.MirrorCS", {"start": v(61.46, -328.8) * mm, "end": v(61.46, -201.8) * mm});
            skLineSegment(sketch, "E247.MirrorCS", {"start": v(843.96, -328.8) * mm, "end": v(843.96, -201.8) * mm});
            skLineSegment(sketch, "E248.MirrorCS", {"start": v(420.2, -328.8) * mm, "end": v(420.2, -201.8) * mm});
            skLineSegment(sketch, "E249.MirrorCS", {"start": v(518.06, -328.8) * mm, "end": v(518.06, -201.8) * mm});
            skLineSegment(sketch, "E250.MirrorCS", {"start": v(173.24, -328.8) * mm, "end": v(173.24, -201.8) * mm});
            skLineSegment(sketch, "E251.MirrorCS", {"start": v(165.62, -328.8) * mm, "end": v(165.62, -201.8) * mm});
            skLineSegment(sketch, "E252.MirrorCS", {"start": v(510.44, -328.8) * mm, "end": v(510.44, -201.8) * mm});
            skLineSegment(sketch, "E253.MirrorCS", {"start": v(4.65, -328.8) * mm, "end": v(4.65, -201.8) * mm});
            skLineSegment(sketch, "E254.MirrorCS", {"start": v(851.58, -328.8) * mm, "end": v(851.58, -201.8) * mm});
            skLineSegment(sketch, "E255.MirrorCS", {"start": v(427.82, -328.8) * mm, "end": v(427.82, -201.8) * mm});
            skLineSegment(sketch, "E256.MirrorCS", {"start": v(208.8, -328.8) * mm, "end": v(208.8, -201.8) * mm});
            skLineSegment(sketch, "E257.MirrorCS", {"start": v(69.08, -328.8) * mm, "end": v(69.08, -201.8) * mm});
            skLineSegment(sketch, "E258.MirrorCS", {"start": v(112.26, -328.8) * mm, "end": v(112.26, -201.8) * mm});
            skLineSegment(sketch, "E259.MirrorCS", {"start": v(561.24, -328.8) * mm, "end": v(561.24, -201.8) * mm});
            skLineSegment(sketch, "E260.MirrorCS", {"start": v(-30.9, -328.8) * mm, "end": v(-30.9, -201.8) * mm});
            skLineSegment(sketch, "E261.MirrorCS", {"start": v(370.67, -201.8) * mm, "end": v(370.67, -328.8) * mm});
            skLineSegment(sketch, "E262.MirrorCS", {"start": v(434.17, -328.8) * mm, "end": v(434.17, -201.8) * mm});
            skLineSegment(sketch, "E263.MirrorCS", {"start": v(384.64, -328.8) * mm, "end": v(384.64, -201.8) * mm});
            skLineSegment(sketch, "E264.MirrorCS", {"start": v(216.42, -328.8) * mm, "end": v(216.42, -201.8) * mm});
            skLineSegment(sketch, "E265.MirrorCS", {"start": v(800.78, -328.8) * mm, "end": v(800.78, -201.8) * mm});
            skLineSegment(sketch, "E266.MirrorCS", {"start": v(553.62, -328.8) * mm, "end": v(553.62, -201.8) * mm});
            skLineSegment(sketch, "E267.MirrorCS", {"start": v(808.4, -328.8) * mm, "end": v(808.4, -201.8) * mm});
            skLineSegment(sketch, "E268.MirrorCS", {"start": v(104.64, -328.8) * mm, "end": v(104.64, -201.8) * mm});
            skLineSegment(sketch, "E269.MirrorCS", {"start": v(567.6, -201.8) * mm, "end": v(567.6, -328.8) * mm});
            skLineSegment(sketch, "E270.MirrorCS", {"start": v(504.1, -328.8) * mm, "end": v(504.1, -201.8) * mm});
            skLineSegment(sketch, "E271.MirrorCS", {"start": v(222.77, -201.8) * mm, "end": v(222.77, -328.8) * mm});
            skLineSegment(sketch, "E272.0", {"start": v(922.66, 120.17) * mm, "end": v(922.66, -61.86) * mm});
            skLineSegment(sketch, "E273.MirrorCS", {"start": v(993.74, -36.28) * mm, "end": v(1001.36, -36.28) * mm});
            skLineSegment(sketch, "E274.MirrorCS", {"start": v(1001.36, 90.72) * mm, "end": v(993.74, 90.72) * mm});
            skLineSegment(sketch, "E275.MirrorCS", {"start": v(1036.92, -36.28) * mm, "end": v(1044.54, -36.28) * mm});
            skLineSegment(sketch, "E276.MirrorCS", {"start": v(1036.92, 90.72) * mm, "end": v(1044.54, 90.72) * mm});
            skLineSegment(sketch, "E277.MirrorCS", {"start": v(1044.54, 90.72) * mm, "end": v(1044.54, -36.28) * mm});
            skLineSegment(sketch, "E278.MirrorCS", {"start": v(1036.92, 90.72) * mm, "end": v(1036.92, -36.28) * mm});
            skLineSegment(sketch, "E279.MirrorCS", {"start": v(1001.36, 90.72) * mm, "end": v(1001.36, -36.28) * mm});
            skLineSegment(sketch, "E280.MirrorCS", {"start": v(993.74, 90.72) * mm, "end": v(993.74, -36.28) * mm});
            skSolve(sketch);
        }
        {
            var Q0;
            Q0=qSketchRegion(id+"F2",true);
            extrude(context, id + "F3", {"entities" : qUnion([Q0]), "operationType" : NewBodyOperationType.REMOVE, "oppositeDirection" : true, "depth" : 0.63 * mm});
        }
        {
            var Q0;
            Q0=makeQuery(id+"F1.opExtrude","CAP_EDGE",EDGE,{"disambiguationData":[OSD([sQuery(id+"F0.wireOp",EDGE,"E0")])],"isStart":false});
            var Q1;
            Q1=makeQuery(id+"F1.opExtrude","CAP_EDGE",EDGE,{"disambiguationData":[OSD([sQuery(id+"F0.wireOp",EDGE,"E2")])],"isStart":false});
            var Q2;
            Q2=makeQuery(id+"F1.opExtrude","CAP_EDGE",EDGE,{"disambiguationData":[OSD([sQuery(id+"F0.wireOp",EDGE,"E19.MirrorCS")])],"isStart":false});
            var Q3;
            Q3=makeQuery(id+"F1.opExtrude","CAP_EDGE",EDGE,{"disambiguationData":[OSD([sQuery(id+"F0.wireOp",EDGE,"E14.MirrorCS")])],"isStart":false});
            var Q4;
            Q4=makeQuery(id+"F1.opExtrude","CAP_EDGE",EDGE,{"disambiguationData":[OSD([sQuery(id+"F0.wireOp",EDGE,"E35.MirrorCS")])],"isStart":false});
            var Q5;
            Q5=makeQuery(id+"F1.opExtrude","CAP_EDGE",EDGE,{"disambiguationData":[OSD([sQuery(id+"F0.wireOp",EDGE,"E33.MirrorCS")])],"isStart":false});
            var Q6;
            Q6=makeQuery(id+"F1.opExtrude","CAP_EDGE",EDGE,{"disambiguationData":[OSD([sQuery(id+"F0.wireOp",EDGE,"E45.MirrorCS")])],"isStart":false});
            var Q7;
            Q7=makeQuery(id+"F1.opExtrude","CAP_EDGE",EDGE,{"disambiguationData":[OSD([sQuery(id+"F0.wireOp",EDGE,"E47.MirrorCS")])],"isStart":false});
            var Q8;
            Q8=makeQuery(id+"F1.opExtrude","CAP_EDGE",EDGE,{"disambiguationData":[OSD([sQuery(id+"F0.wireOp",EDGE,"E57.MirrorCS")])],"isStart":false});
            var Q9;
            Q9=makeQuery(id+"F1.opExtrude","CAP_EDGE",EDGE,{"disambiguationData":[OSD([sQuery(id+"F0.wireOp",EDGE,"E58.MirrorCS")])],"isStart":false});
            fillet(context, id + "F4", {"entities" : qUnion([Q0, Q1, Q2, Q3, Q4, Q5, Q6, Q7, Q8, Q9]), "radius" : 5.08 * mm, "tangentPropagation" : true, "allowEdgeOverflow" : false});
        }
    });
